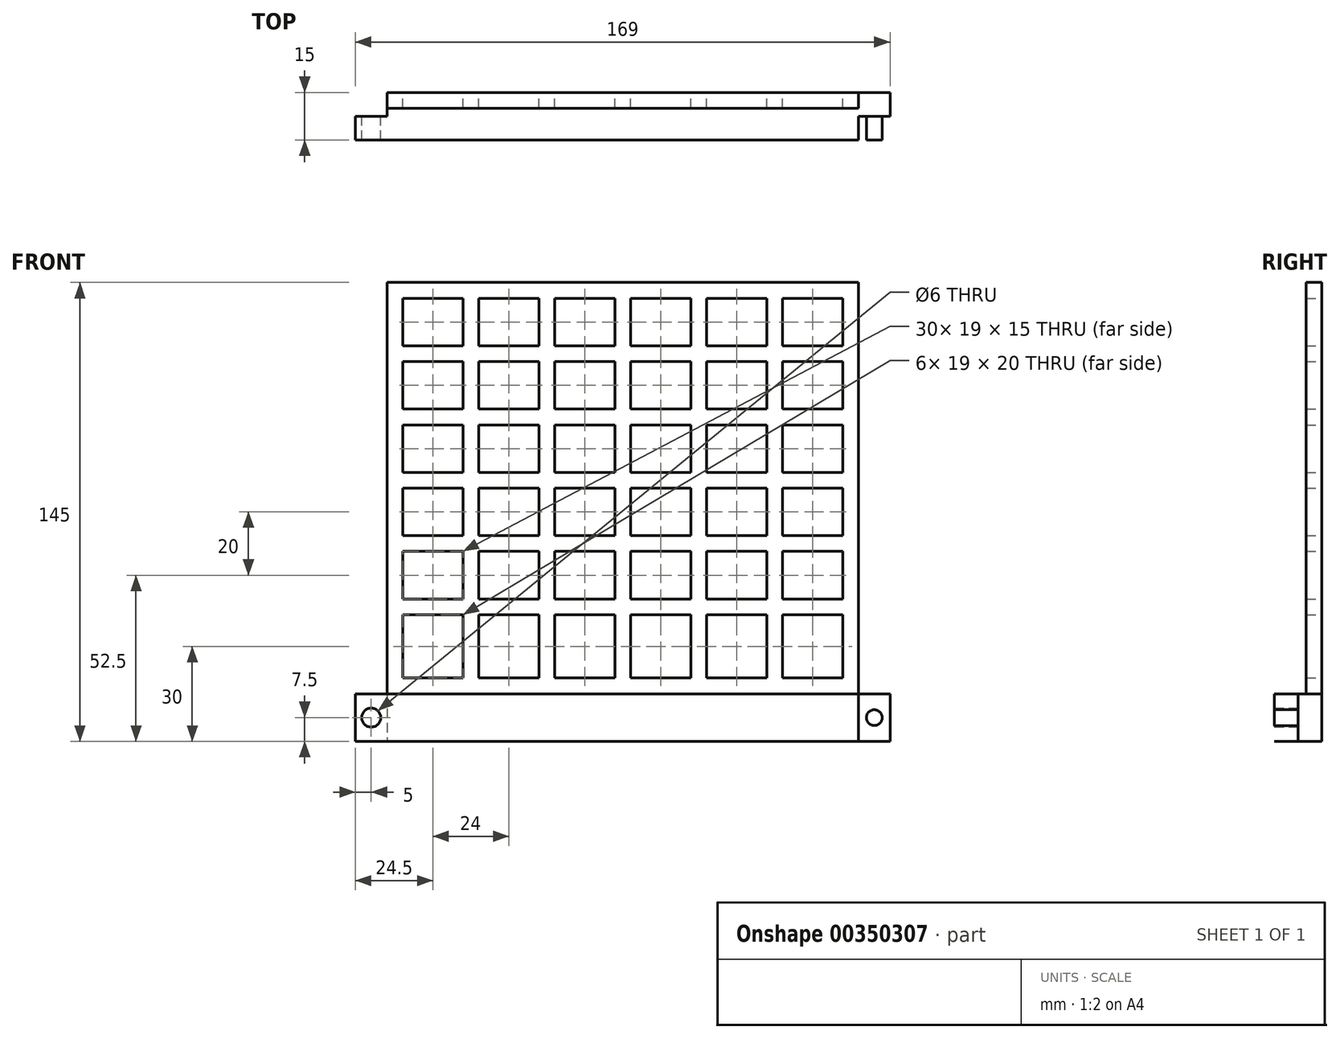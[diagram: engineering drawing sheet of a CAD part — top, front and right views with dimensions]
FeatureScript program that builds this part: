
annotation { "Feature Type Name" : "Feature", "Feature Type Description" : "" }
export const myFeature = defineFeature(function(context is Context, id is Id, definition is map)
    precondition{}
    {
        {
            var Q0;
            Q0=qCreatedBy(makeId("Front.planeOp"),FACE);
            var sketch = newSketch(context, id + "F0", { "sketchPlane" : qUnion([Q0])});
            skLineSegment(sketch, "E0.bottom", {"start": v(0, 0) * mm, "end": v(149, 0) * mm});
            skLineSegment(sketch, "E1.0.5.1", {"start": v(149, 145) * mm, "end": v(0, 145) * mm});
            skLineSegment(sketch, "E2.right", {"start": v(5, 140) * mm, "end": v(5, 125) * mm});
            skLineSegment(sketch, "E3.1.0.1", {"start": v(29, 140) * mm, "end": v(29, 125) * mm});
            skLineSegment(sketch, "E3.1.0.2", {"start": v(24, 140) * mm, "end": v(24, 125) * mm});
            skLineSegment(sketch, "E3.2.0.1", {"start": v(53, 140) * mm, "end": v(53, 125) * mm});
            skLineSegment(sketch, "E3.2.0.2", {"start": v(48, 140) * mm, "end": v(48, 125) * mm});
            skLineSegment(sketch, "E3.3.0.1", {"start": v(77, 140) * mm, "end": v(77, 125) * mm});
            skLineSegment(sketch, "E3.3.0.2", {"start": v(72, 140) * mm, "end": v(72, 125) * mm});
            skLineSegment(sketch, "E3.4.0.1", {"start": v(101, 140) * mm, "end": v(101, 125) * mm});
            skLineSegment(sketch, "E3.4.0.2", {"start": v(96, 140) * mm, "end": v(96, 125) * mm});
            skLineSegment(sketch, "E3.5.0.1", {"start": v(125, 140) * mm, "end": v(125, 125) * mm});
            skLineSegment(sketch, "E3.5.0.2", {"start": v(120, 140) * mm, "end": v(120, 125) * mm});
            skLineSegment(sketch, "E3.6.0.2", {"start": v(144, 140) * mm, "end": v(144, 125) * mm});
            skLineSegment(sketch, "E3.direction1", {"start": v(5, 20) * mm, "end": v(24, 20) * mm, "construction": true});
            skLineSegment(sketch, "E4.trimOffspring", {"start": v(5, 60) * mm, "end": v(5, 45) * mm});
            skLineSegment(sketch, "E5.trimOffspring", {"start": v(5, 40) * mm, "end": v(5, 20) * mm});
            skLineSegment(sketch, "E6.trimOffspring", {"start": v(24, 40) * mm, "end": v(24, 20) * mm});
            skLineSegment(sketch, "E7.trimOffspring", {"start": v(29, 40) * mm, "end": v(29, 20) * mm});
            skLineSegment(sketch, "E8.trimOffspring", {"start": v(24, 45) * mm, "end": v(5, 45) * mm});
            skLineSegment(sketch, "E9.trimOffspring", {"start": v(24, 40) * mm, "end": v(5, 40) * mm});
            skLineSegment(sketch, "E10.trimOffspring", {"start": v(48, 40) * mm, "end": v(48, 20) * mm});
            skLineSegment(sketch, "E11.trimOffspring", {"start": v(53, 40) * mm, "end": v(53, 20) * mm});
            skLineSegment(sketch, "E12.trimOffspring", {"start": v(48, 45) * mm, "end": v(29, 45) * mm});
            skLineSegment(sketch, "E13.trimOffspring", {"start": v(48, 40) * mm, "end": v(29, 40) * mm});
            skLineSegment(sketch, "E14.trimOffspring", {"start": v(29, 20) * mm, "end": v(48, 20) * mm});
            skLineSegment(sketch, "E15.trimOffspring", {"start": v(77, 20) * mm, "end": v(96, 20) * mm});
            skLineSegment(sketch, "E16.trimOffspring", {"start": v(72, 40) * mm, "end": v(53, 40) * mm});
            skLineSegment(sketch, "E17.trimOffspring", {"start": v(72, 40) * mm, "end": v(72, 20) * mm});
            skLineSegment(sketch, "E18.trimOffspring", {"start": v(72, 45) * mm, "end": v(53, 45) * mm});
            skLineSegment(sketch, "E19.trimOffspring", {"start": v(77, 40) * mm, "end": v(77, 20) * mm});
            skLineSegment(sketch, "E20.trimOffspring", {"start": v(72, 60) * mm, "end": v(53, 60) * mm});
            skLineSegment(sketch, "E21", {"start": v(5, 20) * mm, "end": v(24, 20) * mm});
            skLineSegment(sketch, "E22", {"start": v(53, 20) * mm, "end": v(72, 20) * mm});
            skLineSegment(sketch, "E23.trimOffspring", {"start": v(101, 20) * mm, "end": v(120, 20) * mm});
            skLineSegment(sketch, "E24.trimOffspring", {"start": v(125, 20) * mm, "end": v(144, 20) * mm});
            skLineSegment(sketch, "E25.trimOffspring", {"start": v(144, 40) * mm, "end": v(125, 40) * mm});
            skLineSegment(sketch, "E26.trimOffspring", {"start": v(144, 45) * mm, "end": v(125, 45) * mm});
            skLineSegment(sketch, "E27.trimOffspring", {"start": v(144, 40) * mm, "end": v(144, 20) * mm});
            skLineSegment(sketch, "E28.trimOffspring", {"start": v(125, 40) * mm, "end": v(125, 20) * mm});
            skLineSegment(sketch, "E29.trimOffspring", {"start": v(120, 40) * mm, "end": v(120, 20) * mm});
            skLineSegment(sketch, "E30.trimOffspring", {"start": v(120, 45) * mm, "end": v(101, 45) * mm});
            skLineSegment(sketch, "E31.trimOffspring", {"start": v(120, 40) * mm, "end": v(101, 40) * mm});
            skLineSegment(sketch, "E32.trimOffspring", {"start": v(96, 40) * mm, "end": v(96, 20) * mm});
            skLineSegment(sketch, "E33.trimOffspring", {"start": v(96, 45) * mm, "end": v(77, 45) * mm});
            skLineSegment(sketch, "E34.trimOffspring", {"start": v(101, 40) * mm, "end": v(101, 20) * mm});
            skLineSegment(sketch, "E35.trimOffspring", {"start": v(96, 40) * mm, "end": v(77, 40) * mm});
            skLineSegment(sketch, "E36.trimOffspring", {"start": v(96, 60) * mm, "end": v(77, 60) * mm});
            skLineSegment(sketch, "E37.trimOffspring", {"start": v(96, 60) * mm, "end": v(96, 45) * mm});
            skLineSegment(sketch, "E38.trimOffspring", {"start": v(96, 65) * mm, "end": v(77, 65) * mm});
            skLineSegment(sketch, "E39.trimOffspring", {"start": v(101, 60) * mm, "end": v(101, 45) * mm});
            skLineSegment(sketch, "E40.trimOffspring", {"start": v(120, 60) * mm, "end": v(120, 45) * mm});
            skLineSegment(sketch, "E41.trimOffspring", {"start": v(120, 65) * mm, "end": v(101, 65) * mm});
            skLineSegment(sketch, "E42.trimOffspring", {"start": v(125, 60) * mm, "end": v(125, 45) * mm});
            skLineSegment(sketch, "E43.trimOffspring", {"start": v(120, 60) * mm, "end": v(101, 60) * mm});
            skLineSegment(sketch, "E44.trimOffspring", {"start": v(144, 60) * mm, "end": v(144, 45) * mm});
            skLineSegment(sketch, "E45.trimOffspring", {"start": v(144, 65) * mm, "end": v(125, 65) * mm});
            skLineSegment(sketch, "E46.trimOffspring", {"start": v(144, 60) * mm, "end": v(125, 60) * mm});
            skLineSegment(sketch, "E47.trimOffspring", {"start": v(144, 80) * mm, "end": v(125, 80) * mm});
            skLineSegment(sketch, "E48.trimOffspring", {"start": v(144, 80) * mm, "end": v(144, 65) * mm});
            skLineSegment(sketch, "E49.trimOffspring", {"start": v(144, 85) * mm, "end": v(125, 85) * mm});
            skLineSegment(sketch, "E50.trimOffspring", {"start": v(72, 65) * mm, "end": v(53, 65) * mm});
            skLineSegment(sketch, "E51.trimOffspring", {"start": v(77, 60) * mm, "end": v(77, 45) * mm});
            skLineSegment(sketch, "E52.trimOffspring", {"start": v(72, 60) * mm, "end": v(72, 45) * mm});
            skLineSegment(sketch, "E53.trimOffspring", {"start": v(53, 60) * mm, "end": v(53, 45) * mm});
            skLineSegment(sketch, "E54.trimOffspring", {"start": v(48, 60) * mm, "end": v(48, 45) * mm});
            skLineSegment(sketch, "E55.trimOffspring", {"start": v(48, 65) * mm, "end": v(29, 65) * mm});
            skLineSegment(sketch, "E56.trimOffspring", {"start": v(48, 60) * mm, "end": v(29, 60) * mm});
            skLineSegment(sketch, "E57.trimOffspring", {"start": v(29, 60) * mm, "end": v(29, 45) * mm});
            skLineSegment(sketch, "E58.trimOffspring", {"start": v(24, 60) * mm, "end": v(24, 45) * mm});
            skLineSegment(sketch, "E59.trimOffspring", {"start": v(24, 65) * mm, "end": v(5, 65) * mm});
            skLineSegment(sketch, "E60.trimOffspring", {"start": v(24, 60) * mm, "end": v(5, 60) * mm});
            skLineSegment(sketch, "E61.trimOffspring", {"start": v(125, 80) * mm, "end": v(125, 65) * mm});
            skLineSegment(sketch, "E62.trimOffspring", {"start": v(120, 80) * mm, "end": v(120, 65) * mm});
            skLineSegment(sketch, "E63.trimOffspring", {"start": v(120, 85) * mm, "end": v(101, 85) * mm});
            skLineSegment(sketch, "E64.trimOffspring", {"start": v(120, 80) * mm, "end": v(101, 80) * mm});
            skLineSegment(sketch, "E65.trimOffspring", {"start": v(101, 80) * mm, "end": v(101, 65) * mm});
            skLineSegment(sketch, "E66.trimOffspring", {"start": v(96, 80) * mm, "end": v(96, 65) * mm});
            skLineSegment(sketch, "E67.trimOffspring", {"start": v(96, 85) * mm, "end": v(77, 85) * mm});
            skLineSegment(sketch, "E68.trimOffspring", {"start": v(96, 80) * mm, "end": v(77, 80) * mm});
            skLineSegment(sketch, "E69.trimOffspring", {"start": v(72, 80) * mm, "end": v(72, 65) * mm});
            skLineSegment(sketch, "E70.trimOffspring", {"start": v(72, 85) * mm, "end": v(53, 85) * mm});
            skLineSegment(sketch, "E71.trimOffspring", {"start": v(77, 80) * mm, "end": v(77, 65) * mm});
            skLineSegment(sketch, "E72.trimOffspring", {"start": v(72, 80) * mm, "end": v(53, 80) * mm});
            skLineSegment(sketch, "E73.trimOffspring", {"start": v(48, 80) * mm, "end": v(48, 65) * mm});
            skLineSegment(sketch, "E74.trimOffspring", {"start": v(48, 85) * mm, "end": v(29, 85) * mm});
            skLineSegment(sketch, "E75.trimOffspring", {"start": v(53, 80) * mm, "end": v(53, 65) * mm});
            skLineSegment(sketch, "E76.trimOffspring", {"start": v(48, 80) * mm, "end": v(29, 80) * mm});
            skLineSegment(sketch, "E77.trimOffspring", {"start": v(24, 80) * mm, "end": v(24, 65) * mm});
            skLineSegment(sketch, "E78.trimOffspring", {"start": v(24, 85) * mm, "end": v(5, 85) * mm});
            skLineSegment(sketch, "E79.trimOffspring", {"start": v(29, 80) * mm, "end": v(29, 65) * mm});
            skLineSegment(sketch, "E80.trimOffspring", {"start": v(24, 80) * mm, "end": v(5, 80) * mm});
            skLineSegment(sketch, "E81.trimOffspring", {"start": v(5, 80) * mm, "end": v(5, 65) * mm});
            skLineSegment(sketch, "E82.trimOffspring", {"start": v(5, 100) * mm, "end": v(5, 85) * mm});
            skLineSegment(sketch, "E83.trimOffspring", {"start": v(24, 100) * mm, "end": v(24, 85) * mm});
            skLineSegment(sketch, "E84.trimOffspring", {"start": v(24, 105) * mm, "end": v(5, 105) * mm});
            skLineSegment(sketch, "E85.trimOffspring", {"start": v(29, 100) * mm, "end": v(29, 85) * mm});
            skLineSegment(sketch, "E86.trimOffspring", {"start": v(24, 100) * mm, "end": v(5, 100) * mm});
            skLineSegment(sketch, "E87.trimOffspring", {"start": v(48, 100) * mm, "end": v(48, 85) * mm});
            skLineSegment(sketch, "E88.trimOffspring", {"start": v(48, 105) * mm, "end": v(29, 105) * mm});
            skLineSegment(sketch, "E89.trimOffspring", {"start": v(53, 100) * mm, "end": v(53, 85) * mm});
            skLineSegment(sketch, "E90.trimOffspring", {"start": v(48, 100) * mm, "end": v(29, 100) * mm});
            skLineSegment(sketch, "E91.trimOffspring", {"start": v(72, 100) * mm, "end": v(72, 85) * mm});
            skLineSegment(sketch, "E92.trimOffspring", {"start": v(72, 105) * mm, "end": v(53, 105) * mm});
            skLineSegment(sketch, "E93.trimOffspring", {"start": v(77, 100) * mm, "end": v(77, 85) * mm});
            skLineSegment(sketch, "E94.trimOffspring", {"start": v(72, 100) * mm, "end": v(53, 100) * mm});
            skLineSegment(sketch, "E95.trimOffspring", {"start": v(96, 100) * mm, "end": v(96, 85) * mm});
            skLineSegment(sketch, "E96.trimOffspring", {"start": v(96, 105) * mm, "end": v(77, 105) * mm});
            skLineSegment(sketch, "E97.trimOffspring", {"start": v(101, 100) * mm, "end": v(101, 85) * mm});
            skLineSegment(sketch, "E98.trimOffspring", {"start": v(96, 100) * mm, "end": v(77, 100) * mm});
            skLineSegment(sketch, "E99.trimOffspring", {"start": v(120, 100) * mm, "end": v(120, 85) * mm});
            skLineSegment(sketch, "E100.trimOffspring", {"start": v(120, 105) * mm, "end": v(101, 105) * mm});
            skLineSegment(sketch, "E101.trimOffspring", {"start": v(125, 100) * mm, "end": v(125, 85) * mm});
            skLineSegment(sketch, "E102.trimOffspring", {"start": v(120, 100) * mm, "end": v(101, 100) * mm});
            skLineSegment(sketch, "E103.trimOffspring", {"start": v(144, 100) * mm, "end": v(144, 85) * mm});
            skLineSegment(sketch, "E104.trimOffspring", {"start": v(144, 105) * mm, "end": v(125, 105) * mm});
            skLineSegment(sketch, "E105.trimOffspring", {"start": v(144, 100) * mm, "end": v(125, 100) * mm});
            skLineSegment(sketch, "E106.trimOffspring", {"start": v(120, 120) * mm, "end": v(101, 120) * mm});
            skLineSegment(sketch, "E107.trimOffspring", {"start": v(96, 120) * mm, "end": v(77, 120) * mm});
            skLineSegment(sketch, "E108.trimOffspring", {"start": v(72, 120) * mm, "end": v(53, 120) * mm});
            skLineSegment(sketch, "E109.trimOffspring", {"start": v(48, 120) * mm, "end": v(29, 120) * mm});
            skLineSegment(sketch, "E110.trimOffspring", {"start": v(24, 120) * mm, "end": v(5, 120) * mm});
            skLineSegment(sketch, "E111.trimOffspring", {"start": v(5, 120) * mm, "end": v(5, 105) * mm});
            skLineSegment(sketch, "E112.trimOffspring", {"start": v(24, 120) * mm, "end": v(24, 105) * mm});
            skLineSegment(sketch, "E113.trimOffspring", {"start": v(29, 120) * mm, "end": v(29, 105) * mm});
            skLineSegment(sketch, "E114.trimOffspring", {"start": v(48, 120) * mm, "end": v(48, 105) * mm});
            skLineSegment(sketch, "E115.trimOffspring", {"start": v(53, 120) * mm, "end": v(53, 105) * mm});
            skLineSegment(sketch, "E116.trimOffspring", {"start": v(72, 120) * mm, "end": v(72, 105) * mm});
            skLineSegment(sketch, "E117.trimOffspring", {"start": v(77, 120) * mm, "end": v(77, 105) * mm});
            skLineSegment(sketch, "E118.trimOffspring", {"start": v(96, 120) * mm, "end": v(96, 105) * mm});
            skLineSegment(sketch, "E119.trimOffspring", {"start": v(101, 120) * mm, "end": v(101, 105) * mm});
            skLineSegment(sketch, "E120.trimOffspring", {"start": v(120, 120) * mm, "end": v(120, 105) * mm});
            skLineSegment(sketch, "E121.trimOffspring", {"start": v(125, 120) * mm, "end": v(125, 105) * mm});
            skLineSegment(sketch, "E122.trimOffspring", {"start": v(144, 120) * mm, "end": v(144, 105) * mm});
            skLineSegment(sketch, "E123.trimOffspring", {"start": v(144, 120) * mm, "end": v(125, 120) * mm});
            skLineSegment(sketch, "E124.trimOffspring", {"start": v(24, 140) * mm, "end": v(5, 140) * mm});
            skLineSegment(sketch, "E125.trimOffspring", {"start": v(48, 140) * mm, "end": v(29, 140) * mm});
            skLineSegment(sketch, "E126.trimOffspring", {"start": v(72, 140) * mm, "end": v(53, 140) * mm});
            skLineSegment(sketch, "E127.trimOffspring", {"start": v(96, 140) * mm, "end": v(77, 140) * mm});
            skLineSegment(sketch, "E128.trimOffspring", {"start": v(120, 140) * mm, "end": v(101, 140) * mm});
            skLineSegment(sketch, "E129.trimOffspring", {"start": v(144, 140) * mm, "end": v(125, 140) * mm});
            skLineSegment(sketch, "E130.trimOffspring", {"start": v(24, 125) * mm, "end": v(5, 125) * mm});
            skLineSegment(sketch, "E131.trimOffspring", {"start": v(144, 125) * mm, "end": v(125, 125) * mm});
            skLineSegment(sketch, "E132", {"start": v(29, 125) * mm, "end": v(48, 125) * mm});
            skLineSegment(sketch, "E133", {"start": v(53, 125) * mm, "end": v(72, 125) * mm});
            skLineSegment(sketch, "E134", {"start": v(77, 125) * mm, "end": v(96, 125) * mm});
            skLineSegment(sketch, "E135", {"start": v(101, 125) * mm, "end": v(120, 125) * mm});
            skLineSegment(sketch, "E136", {"start": v(0, 145) * mm, "end": v(0, 0) * mm});
            skLineSegment(sketch, "E137", {"start": v(149, 0) * mm, "end": v(149, 145) * mm});
            skSolve(sketch);
        }
        {
            var Q0;
            Q0 = qSketchRegion(id + "F0", true);
            extrude(context, id + "F1", {"entities" : qUnion([Q0]), "depth" : 5 * mm});
        }
        {
            var Q0;
            Q0=makeQuery(id+"F1.opExtrude","CAP_FACE",FACE,{"disambiguationData":[OSD([sQuery(id+"F0.wireOp",EDGE,"E0.bottom"),sQuery(id+"F0.wireOp",EDGE,"E1.0.5.1"),sQuery(id+"F0.wireOp",EDGE,"E2.right"),sQuery(id+"F0.wireOp",EDGE,"E3.1.0.1"),sQuery(id+"F0.wireOp",EDGE,"E3.1.0.2"),sQuery(id+"F0.wireOp",EDGE,"E3.2.0.1"),sQuery(id+"F0.wireOp",EDGE,"E3.2.0.2"),sQuery(id+"F0.wireOp",EDGE,"E3.3.0.1"),sQuery(id+"F0.wireOp",EDGE,"E3.3.0.2"),sQuery(id+"F0.wireOp",EDGE,"E3.4.0.1"),sQuery(id+"F0.wireOp",EDGE,"E3.4.0.2"),sQuery(id+"F0.wireOp",EDGE,"E3.5.0.1"),sQuery(id+"F0.wireOp",EDGE,"E3.5.0.2"),sQuery(id+"F0.wireOp",EDGE,"E3.6.0.2"),sQuery(id+"F0.wireOp",EDGE,"E4.trimOffspring"),sQuery(id+"F0.wireOp",EDGE,"E5.trimOffspring"),sQuery(id+"F0.wireOp",EDGE,"E6.trimOffspring"),sQuery(id+"F0.wireOp",EDGE,"E7.trimOffspring"),sQuery(id+"F0.wireOp",EDGE,"E8.trimOffspring"),sQuery(id+"F0.wireOp",EDGE,"E9.trimOffspring"),sQuery(id+"F0.wireOp",EDGE,"E10.trimOffspring"),sQuery(id+"F0.wireOp",EDGE,"E11.trimOffspring"),sQuery(id+"F0.wireOp",EDGE,"E12.trimOffspring"),sQuery(id+"F0.wireOp",EDGE,"E13.trimOffspring"),sQuery(id+"F0.wireOp",EDGE,"E14.trimOffspring"),sQuery(id+"F0.wireOp",EDGE,"E15.trimOffspring"),sQuery(id+"F0.wireOp",EDGE,"E16.trimOffspring"),sQuery(id+"F0.wireOp",EDGE,"E17.trimOffspring"),sQuery(id+"F0.wireOp",EDGE,"E18.trimOffspring"),sQuery(id+"F0.wireOp",EDGE,"E19.trimOffspring"),sQuery(id+"F0.wireOp",EDGE,"E20.trimOffspring"),sQuery(id+"F0.wireOp",EDGE,"E21"),sQuery(id+"F0.wireOp",EDGE,"E22"),sQuery(id+"F0.wireOp",EDGE,"E23.trimOffspring"),sQuery(id+"F0.wireOp",EDGE,"E24.trimOffspring"),sQuery(id+"F0.wireOp",EDGE,"E25.trimOffspring"),sQuery(id+"F0.wireOp",EDGE,"E26.trimOffspring"),sQuery(id+"F0.wireOp",EDGE,"E27.trimOffspring"),sQuery(id+"F0.wireOp",EDGE,"E28.trimOffspring"),sQuery(id+"F0.wireOp",EDGE,"E29.trimOffspring"),sQuery(id+"F0.wireOp",EDGE,"E30.trimOffspring"),sQuery(id+"F0.wireOp",EDGE,"E31.trimOffspring"),sQuery(id+"F0.wireOp",EDGE,"E32.trimOffspring"),sQuery(id+"F0.wireOp",EDGE,"E33.trimOffspring"),sQuery(id+"F0.wireOp",EDGE,"E34.trimOffspring"),sQuery(id+"F0.wireOp",EDGE,"E35.trimOffspring"),sQuery(id+"F0.wireOp",EDGE,"E36.trimOffspring"),sQuery(id+"F0.wireOp",EDGE,"E37.trimOffspring"),sQuery(id+"F0.wireOp",EDGE,"E38.trimOffspring"),sQuery(id+"F0.wireOp",EDGE,"E39.trimOffspring"),sQuery(id+"F0.wireOp",EDGE,"E40.trimOffspring"),sQuery(id+"F0.wireOp",EDGE,"E41.trimOffspring"),sQuery(id+"F0.wireOp",EDGE,"E42.trimOffspring"),sQuery(id+"F0.wireOp",EDGE,"E43.trimOffspring"),sQuery(id+"F0.wireOp",EDGE,"E44.trimOffspring"),sQuery(id+"F0.wireOp",EDGE,"E45.trimOffspring"),sQuery(id+"F0.wireOp",EDGE,"E46.trimOffspring"),sQuery(id+"F0.wireOp",EDGE,"E47.trimOffspring"),sQuery(id+"F0.wireOp",EDGE,"E48.trimOffspring"),sQuery(id+"F0.wireOp",EDGE,"E49.trimOffspring"),sQuery(id+"F0.wireOp",EDGE,"E50.trimOffspring"),sQuery(id+"F0.wireOp",EDGE,"E51.trimOffspring"),sQuery(id+"F0.wireOp",EDGE,"E52.trimOffspring"),sQuery(id+"F0.wireOp",EDGE,"E53.trimOffspring"),sQuery(id+"F0.wireOp",EDGE,"E54.trimOffspring"),sQuery(id+"F0.wireOp",EDGE,"E55.trimOffspring"),sQuery(id+"F0.wireOp",EDGE,"E56.trimOffspring"),sQuery(id+"F0.wireOp",EDGE,"E57.trimOffspring"),sQuery(id+"F0.wireOp",EDGE,"E58.trimOffspring"),sQuery(id+"F0.wireOp",EDGE,"E59.trimOffspring"),sQuery(id+"F0.wireOp",EDGE,"E60.trimOffspring"),sQuery(id+"F0.wireOp",EDGE,"E61.trimOffspring"),sQuery(id+"F0.wireOp",EDGE,"E62.trimOffspring"),sQuery(id+"F0.wireOp",EDGE,"E63.trimOffspring"),sQuery(id+"F0.wireOp",EDGE,"E64.trimOffspring"),sQuery(id+"F0.wireOp",EDGE,"E65.trimOffspring"),sQuery(id+"F0.wireOp",EDGE,"E66.trimOffspring"),sQuery(id+"F0.wireOp",EDGE,"E67.trimOffspring"),sQuery(id+"F0.wireOp",EDGE,"E68.trimOffspring"),sQuery(id+"F0.wireOp",EDGE,"E69.trimOffspring"),sQuery(id+"F0.wireOp",EDGE,"E70.trimOffspring"),sQuery(id+"F0.wireOp",EDGE,"E71.trimOffspring"),sQuery(id+"F0.wireOp",EDGE,"E72.trimOffspring"),sQuery(id+"F0.wireOp",EDGE,"E73.trimOffspring"),sQuery(id+"F0.wireOp",EDGE,"E74.trimOffspring"),sQuery(id+"F0.wireOp",EDGE,"E75.trimOffspring"),sQuery(id+"F0.wireOp",EDGE,"E76.trimOffspring"),sQuery(id+"F0.wireOp",EDGE,"E77.trimOffspring"),sQuery(id+"F0.wireOp",EDGE,"E78.trimOffspring"),sQuery(id+"F0.wireOp",EDGE,"E79.trimOffspring"),sQuery(id+"F0.wireOp",EDGE,"E80.trimOffspring"),sQuery(id+"F0.wireOp",EDGE,"E81.trimOffspring"),sQuery(id+"F0.wireOp",EDGE,"E82.trimOffspring"),sQuery(id+"F0.wireOp",EDGE,"E83.trimOffspring"),sQuery(id+"F0.wireOp",EDGE,"E84.trimOffspring"),sQuery(id+"F0.wireOp",EDGE,"E85.trimOffspring"),sQuery(id+"F0.wireOp",EDGE,"E86.trimOffspring"),sQuery(id+"F0.wireOp",EDGE,"E87.trimOffspring"),sQuery(id+"F0.wireOp",EDGE,"E88.trimOffspring"),sQuery(id+"F0.wireOp",EDGE,"E89.trimOffspring"),sQuery(id+"F0.wireOp",EDGE,"E90.trimOffspring"),sQuery(id+"F0.wireOp",EDGE,"E91.trimOffspring"),sQuery(id+"F0.wireOp",EDGE,"E92.trimOffspring"),sQuery(id+"F0.wireOp",EDGE,"E93.trimOffspring"),sQuery(id+"F0.wireOp",EDGE,"E94.trimOffspring"),sQuery(id+"F0.wireOp",EDGE,"E95.trimOffspring"),sQuery(id+"F0.wireOp",EDGE,"E96.trimOffspring"),sQuery(id+"F0.wireOp",EDGE,"E97.trimOffspring"),sQuery(id+"F0.wireOp",EDGE,"E98.trimOffspring"),sQuery(id+"F0.wireOp",EDGE,"E99.trimOffspring"),sQuery(id+"F0.wireOp",EDGE,"E100.trimOffspring"),sQuery(id+"F0.wireOp",EDGE,"E101.trimOffspring"),sQuery(id+"F0.wireOp",EDGE,"E102.trimOffspring"),sQuery(id+"F0.wireOp",EDGE,"E103.trimOffspring"),sQuery(id+"F0.wireOp",EDGE,"E104.trimOffspring"),sQuery(id+"F0.wireOp",EDGE,"E105.trimOffspring"),sQuery(id+"F0.wireOp",EDGE,"E106.trimOffspring"),sQuery(id+"F0.wireOp",EDGE,"E107.trimOffspring"),sQuery(id+"F0.wireOp",EDGE,"E108.trimOffspring"),sQuery(id+"F0.wireOp",EDGE,"E109.trimOffspring"),sQuery(id+"F0.wireOp",EDGE,"E110.trimOffspring"),sQuery(id+"F0.wireOp",EDGE,"E111.trimOffspring"),sQuery(id+"F0.wireOp",EDGE,"E112.trimOffspring"),sQuery(id+"F0.wireOp",EDGE,"E113.trimOffspring"),sQuery(id+"F0.wireOp",EDGE,"E114.trimOffspring"),sQuery(id+"F0.wireOp",EDGE,"E115.trimOffspring"),sQuery(id+"F0.wireOp",EDGE,"E116.trimOffspring"),sQuery(id+"F0.wireOp",EDGE,"E117.trimOffspring"),sQuery(id+"F0.wireOp",EDGE,"E118.trimOffspring"),sQuery(id+"F0.wireOp",EDGE,"E119.trimOffspring"),sQuery(id+"F0.wireOp",EDGE,"E120.trimOffspring"),sQuery(id+"F0.wireOp",EDGE,"E121.trimOffspring"),sQuery(id+"F0.wireOp",EDGE,"E122.trimOffspring"),sQuery(id+"F0.wireOp",EDGE,"E123.trimOffspring"),sQuery(id+"F0.wireOp",EDGE,"E124.trimOffspring"),sQuery(id+"F0.wireOp",EDGE,"E125.trimOffspring"),sQuery(id+"F0.wireOp",EDGE,"E126.trimOffspring"),sQuery(id+"F0.wireOp",EDGE,"E127.trimOffspring"),sQuery(id+"F0.wireOp",EDGE,"E128.trimOffspring"),sQuery(id+"F0.wireOp",EDGE,"E129.trimOffspring"),sQuery(id+"F0.wireOp",EDGE,"E130.trimOffspring"),sQuery(id+"F0.wireOp",EDGE,"E131.trimOffspring"),sQuery(id+"F0.wireOp",EDGE,"E132"),sQuery(id+"F0.wireOp",EDGE,"E133"),sQuery(id+"F0.wireOp",EDGE,"E134"),sQuery(id+"F0.wireOp",EDGE,"E135"),sQuery(id+"F0.wireOp",EDGE,"E136"),sQuery(id+"F0.wireOp",EDGE,"E137")])],"isStart":false});
            var sketch = newSketch(context, id + "F2", { "sketchPlane" : qUnion([Q0])});
            skLineSegment(sketch, "E138.bottom", {"start": v(0, 0) * mm, "end": v(149, 0) * mm});
            skLineSegment(sketch, "E138.top", {"start": v(0, 15) * mm, "end": v(149, 15) * mm});
            skLineSegment(sketch, "E138.left", {"start": v(0, 0) * mm, "end": v(0, 15) * mm});
            skLineSegment(sketch, "E138.right", {"start": v(149, 0) * mm, "end": v(149, 15) * mm});
            skSolve(sketch);
        }
        {
            var Q0;
            Q0=makeQuery(id+"F2.imprint","IMPRINT",FACE,{"disambiguationData":[TD([[makeQuery(id+"F2.imprint","IMPRINT",EDGE,{"derivedFrom":sQuery(id+"F2.wireOp",EDGE,"E138.bottom")}),1.0]])]});
            extrude(context, id + "F3", {"entities" : qUnion([Q0]), "operationType" : NewBodyOperationType.ADD, "depth" : 10 * mm});
        }
        {
            var Q0;
            Q0=makeQuery(id+"F3.boolean.opBoolean","MERGE",FACE,{"derivedFrom":[makeQuery(id+"F1.opExtrude","SWEPT_FACE",FACE,{"disambiguationData":[OSD([sQuery(id+"F0.wireOp",EDGE,"E136")])]}),makeQuery(id+"F3.opExtrude","SWEPT_FACE",FACE,{"disambiguationData":[OSD([sQuery(id+"F2.wireOp",EDGE,"E138.left")])]})]});
            var sketch = newSketch(context, id + "F4", { "sketchPlane" : qUnion([Q0])});
            skLineSegment(sketch, "E139.bottom", {"start": v(15, 15) * mm, "end": v(7.5, 15) * mm});
            skLineSegment(sketch, "E139.top", {"start": v(15, 0) * mm, "end": v(7.5, 0) * mm});
            skLineSegment(sketch, "E139.left", {"start": v(15, 15) * mm, "end": v(15, 0) * mm});
            skLineSegment(sketch, "E139.right", {"start": v(7.5, 15) * mm, "end": v(7.5, 0) * mm});
            skSolve(sketch);
        }
        {
            var Q0;
            Q0=makeQuery(id+"F4.imprint","IMPRINT",FACE,{"disambiguationData":[TD([[makeQuery(id+"F4.imprint","IMPRINT",EDGE,{"derivedFrom":sQuery(id+"F4.wireOp",EDGE,"E139.bottom")}),1.0]])]});
            extrude(context, id + "F5", {"entities" : qUnion([Q0]), "operationType" : NewBodyOperationType.ADD, "depth" : 10 * mm});
        }
        {
            var Q0;
            Q0=makeQuery(id+"F5.opExtrude","SWEPT_FACE",FACE,{"disambiguationData":[OSD([sQuery(id+"F4.wireOp",EDGE,"E139.right")])]});
            var sketch = newSketch(context, id + "F6", { "sketchPlane" : qUnion([Q0])});
            skLineSegment(sketch, "E140", {"start": v(5, 15) * mm, "end": v(5, 7.5) * mm, "construction": true});
            skPoint(sketch, "E140.endSnap0", {"position": v(10, 7.5) * mm});
            skCircle(sketch, "E141", {"center": v(5, 7.5) * mm, "radius": 3 * mm});
            skSolve(sketch);
        }
        {
            var Q0;
            Q0=makeQuery(id+"F6.imprint","IMPRINT",FACE,{"disambiguationData":[TD([[makeQuery(id+"F6.imprint","IMPRINT",EDGE,{"derivedFrom":sQuery(id+"F6.wireOp",EDGE,"E141")}),1.0]])]});
            extrude(context, id + "F7", {"entities" : qUnion([Q0]), "operationType" : NewBodyOperationType.REMOVE, "endBound" : BoundingType.UP_TO_NEXT, "oppositeDirection" : true, "depth" : 25 * mm});
        }
        {
            var Q0;
            Q0=makeQuery(id+"F3.boolean.opBoolean","MERGE",FACE,{"derivedFrom":[makeQuery(id+"F1.opExtrude","SWEPT_FACE",FACE,{"disambiguationData":[OSD([sQuery(id+"F0.wireOp",EDGE,"E137")])]}),makeQuery(id+"F3.opExtrude","SWEPT_FACE",FACE,{"disambiguationData":[OSD([sQuery(id+"F2.wireOp",EDGE,"E138.right")])]})]});
            var sketch = newSketch(context, id + "F8", { "sketchPlane" : qUnion([Q0])});
            skLineSegment(sketch, "E142.bottom", {"start": v(-7.5, 0) * mm, "end": v(0, 0) * mm});
            skLineSegment(sketch, "E142.top", {"start": v(-7.5, 15) * mm, "end": v(0, 15) * mm});
            skLineSegment(sketch, "E142.left", {"start": v(-7.5, 0) * mm, "end": v(-7.5, 15) * mm});
            skLineSegment(sketch, "E142.right", {"start": v(0, 0) * mm, "end": v(0, 15) * mm});
            skSolve(sketch);
        }
        {
            var Q0;
            Q0=makeQuery(id+"F8.imprint","IMPRINT",FACE,{"disambiguationData":[TD([[makeQuery(id+"F8.imprint","IMPRINT",EDGE,{"derivedFrom":sQuery(id+"F8.wireOp",EDGE,"E142.bottom")}),1.0]])]});
            extrude(context, id + "F9", {"entities" : qUnion([Q0]), "operationType" : NewBodyOperationType.ADD, "depth" : 10 * mm});
        }
        {
            var Q0;
            Q0=makeQuery(id+"F9.opExtrude","SWEPT_FACE",FACE,{"disambiguationData":[OSD([sQuery(id+"F8.wireOp",EDGE,"E142.left")])]});
            var sketch = newSketch(context, id + "F10", { "sketchPlane" : qUnion([Q0])});
            skCircle(sketch, "E143", {"center": v(154, 7.5) * mm, "radius": 2.5 * mm});
            skPoint(sketch, "E143.centerSnap0", {"position": v(159, 7.5) * mm});
            skPoint(sketch, "E143.centerSnap1", {"position": v(154, 15) * mm});
            skSolve(sketch);
        }
        {
            var Q0;
            Q0=makeQuery(id+"F10.imprint","IMPRINT",FACE,{"disambiguationData":[TD([[makeQuery(id+"F10.imprint","IMPRINT",EDGE,{"derivedFrom":sQuery(id+"F10.wireOp",EDGE,"E143")}),1.0]])]});
            extrude(context, id + "F11", {"entities" : qUnion([Q0]), "operationType" : NewBodyOperationType.ADD, "depth" : 7.5 * mm});
        }
    });
